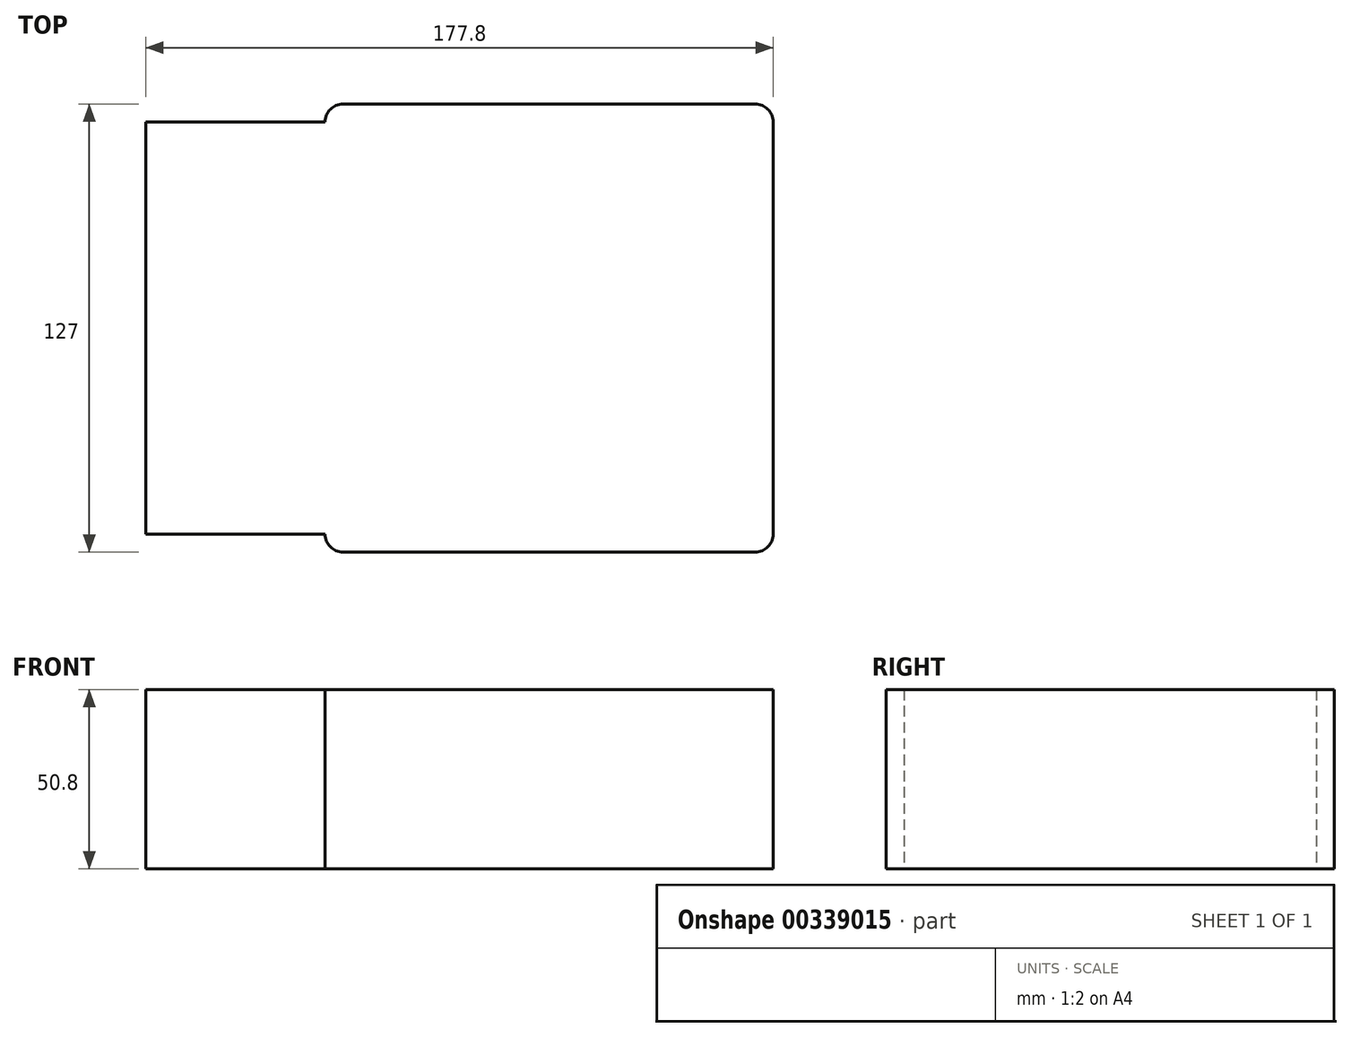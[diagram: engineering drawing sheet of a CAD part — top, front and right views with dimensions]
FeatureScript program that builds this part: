
annotation { "Feature Type Name" : "Feature", "Feature Type Description" : "" }
export const myFeature = defineFeature(function(context is Context, id is Id, definition is map)
    precondition{}
    {
        {
            var Q0;
            Q0=qCreatedBy(makeId("Top.planeOp"),FACE);
            var sketch = newSketch(context, id + "F0", { "sketchPlane" : qUnion([Q0])});
            skLineSegment(sketch, "E0.bottom", {"start": v(-69.64, 69.54) * mm, "end": v(57.36, 69.54) * mm});
            skLineSegment(sketch, "E0.top", {"start": v(-69.64, -57.46) * mm, "end": v(57.36, -57.46) * mm});
            skLineSegment(sketch, "E0.left", {"start": v(-69.64, 69.54) * mm, "end": v(-69.64, -57.46) * mm});
            skLineSegment(sketch, "E0.right", {"start": v(57.36, 69.54) * mm, "end": v(57.36, -57.46) * mm});
            skSolve(sketch);
        }
        {
            var Q0;
            Q0 = qSketchRegion(id + "F0", true);
            extrude(context, id + "F1", {"entities" : qUnion([Q0]), "depth" : 25.4 * mm});
        }
        {
            var Q0;
            Q0=makeQuery(id+"F1.opExtrude","SWEPT_EDGE",EDGE,{"disambiguationData":[OSD([sQuery(id+"F0.wireOp",EDGE,"E0.top"),sQuery(id+"F0.wireOp",EDGE,"E0.right")])]});
            var Q1;
            Q1=makeQuery(id+"F1.opExtrude","SWEPT_EDGE",EDGE,{"disambiguationData":[OSD([sQuery(id+"F0.wireOp",EDGE,"E0.bottom"),sQuery(id+"F0.wireOp",EDGE,"E0.right")])]});
            var Q2;
            Q2=makeQuery(id+"F1.opExtrude","SWEPT_EDGE",EDGE,{"disambiguationData":[OSD([sQuery(id+"F0.wireOp",EDGE,"E0.top"),sQuery(id+"F0.wireOp",EDGE,"E0.left")])]});
            var Q3;
            Q3=makeQuery(id+"F1.opExtrude","SWEPT_EDGE",EDGE,{"disambiguationData":[OSD([sQuery(id+"F0.wireOp",EDGE,"E0.bottom"),sQuery(id+"F0.wireOp",EDGE,"E0.left")])]});
            fillet(context, id + "F2", {"entities" : qUnion([Q0, Q1, Q2, Q3]), "radius" : 5.08 * mm, "tangentPropagation" : true, "allowEdgeOverflow" : false});
        }
        {
            var Q0;
            Q0=makeQuery(id+"F1.opExtrude","SWEPT_FACE",FACE,{"disambiguationData":[OSD([sQuery(id+"F0.wireOp",EDGE,"E0.left")])]});
            extrude(context, id + "F3", {"entities" : qUnion([Q0]), "operationType" : NewBodyOperationType.ADD, "depth" : 25.4 * mm, "offsetDistance" : 25.4 * mm});
        }
        {
            var Q0;
            Q0=makeQuery(id+"F3.opExtrude","CAP_FACE",FACE,{"disambiguationData":[OSD([sQuery(id+"F0.wireOp",EDGE,"E0.left")])],"isStart":false});
            extrude(context, id + "F4", {"entities" : qUnion([Q0]), "operationType" : NewBodyOperationType.ADD, "depth" : 25.4 * mm, "offsetDistance" : 25.4 * mm});
        }
        {
            var Q0;
            Q0=makeQuery(id+"F4.opExtrude","CAP_FACE",FACE,{"disambiguationData":[OSD([sQuery(id+"F0.wireOp",EDGE,"E0.left")])],"isStart":false});
            extrude(context, id + "F5", {"entities" : qUnion([Q0]), "operationType" : NewBodyOperationType.ADD, "oppositeDirection" : true, "depth" : 25.4 * mm, "offsetDistance" : 25.4 * mm});
        }
        {
            var Q0;
            {var subQ0=sQuery(id+"F0.wireOp",EDGE,"E0.left");var subQ1=makeQuery(id+"F1.opExtrude","CAP_EDGE",EDGE,{"disambiguationData":[OSD([subQ0])],"isStart":false});Q0=makeQuery(id+"F4.boolean.opBoolean","MERGE",FACE,{"derivedFrom":[makeQuery(id+"F3.boolean.opBoolean","MERGE",FACE,{"derivedFrom":[makeQuery(id+"F1.opExtrude","CAP_FACE",FACE,{"disambiguationData":[OSD([sQuery(id+"F0.wireOp",EDGE,"E0.bottom"),sQuery(id+"F0.wireOp",EDGE,"E0.top"),subQ0,sQuery(id+"F0.wireOp",EDGE,"E0.right")])],"isStart":false}),makeQuery(id+"F3.opExtrude","SWEPT_FACE",FACE,{"disambiguationData":[OSD([subQ0]),TDD([subQ1])]})]}),makeQuery(id+"F4.opExtrude","SWEPT_FACE",FACE,{"disambiguationData":[OSD([subQ0]),TDD([makeQuery(id+"F3.opExtrude","CAP_EDGE",EDGE,{"disambiguationData":[OSD([subQ0]),TDD([subQ1])],"isStart":false})])]})]});}
            extrude(context, id + "F6", {"entities" : qUnion([Q0]), "operationType" : NewBodyOperationType.ADD, "depth" : 25.4 * mm, "offsetDistance" : 25.4 * mm});
        }
    });
